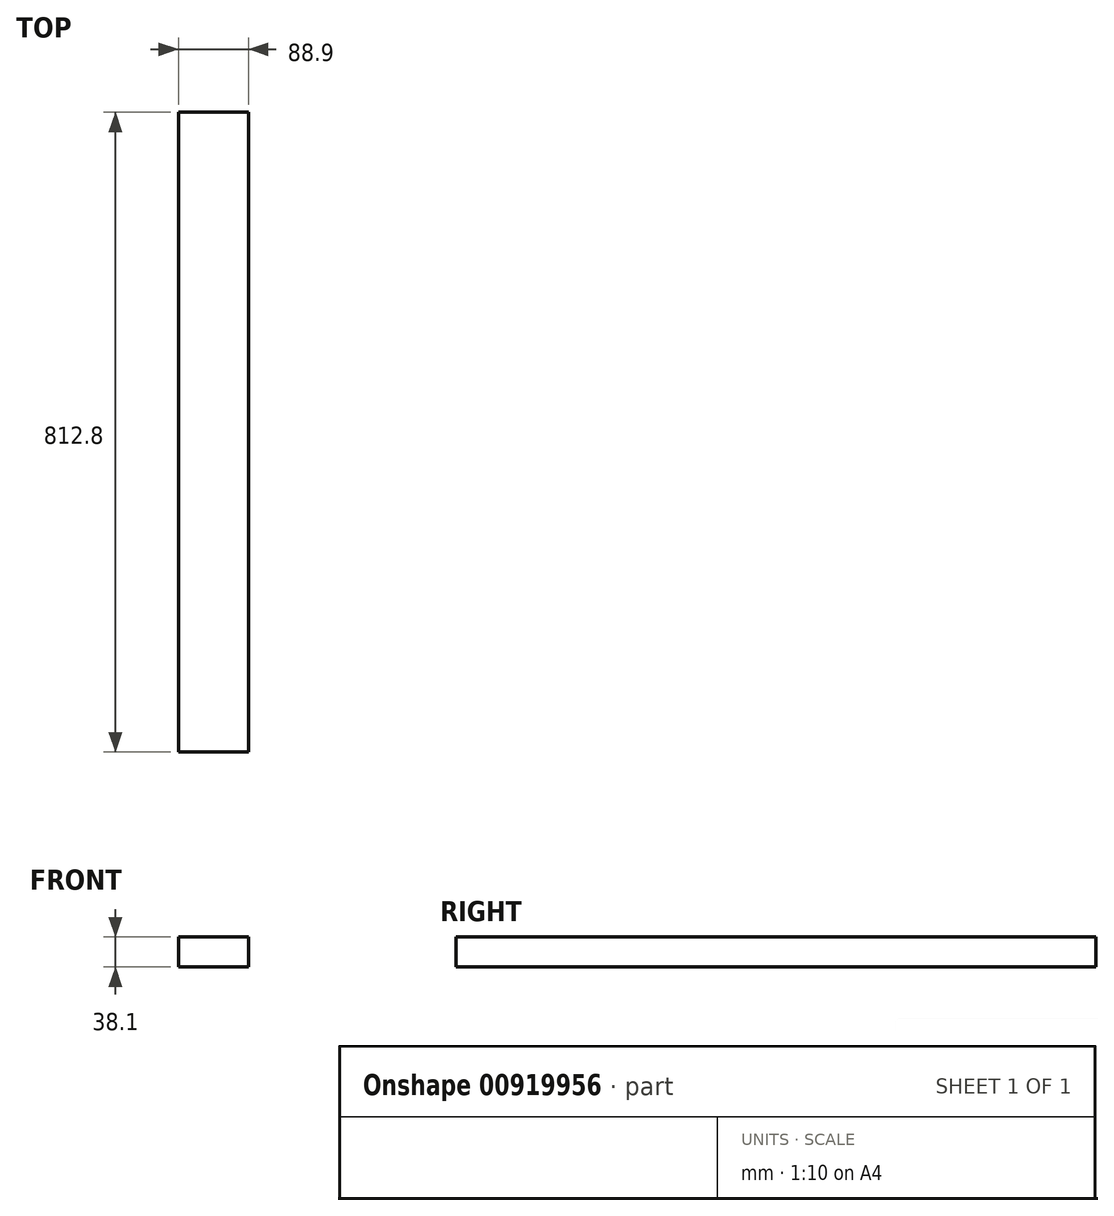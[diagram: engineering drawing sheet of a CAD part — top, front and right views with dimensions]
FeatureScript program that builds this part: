
annotation { "Feature Type Name" : "Feature", "Feature Type Description" : "" }
export const myFeature = defineFeature(function(context is Context, id is Id, definition is map)
    precondition{}
    {
        {
            var Q0;
            Q0=qCreatedBy(makeId("Front.planeOp"),FACE);
            var sketch = newSketch(context, id + "F0", { "sketchPlane" : qUnion([Q0])});
            skLineSegment(sketch, "E0.bottom", {"start": v(44.45, -19.05) * mm, "end": v(-44.45, -19.05) * mm});
            skLineSegment(sketch, "E0.top", {"start": v(44.45, 19.05) * mm, "end": v(-44.45, 19.05) * mm});
            skLineSegment(sketch, "E0.left", {"start": v(44.45, -19.05) * mm, "end": v(44.45, 19.05) * mm});
            skLineSegment(sketch, "E0.right", {"start": v(-44.45, -19.05) * mm, "end": v(-44.45, 19.05) * mm});
            skPoint(sketch, "E0.middle", {"position": v(0, 0) * mm});
            skSolve(sketch);
        }
        {
            var Q0;
            Q0=makeQuery(id+"F0.imprint","IMPRINT",FACE,{"disambiguationData":[TD([[makeQuery(id+"F0.imprint","IMPRINT",EDGE,{"derivedFrom":sQuery(id+"F0.wireOp",EDGE,"E0.bottom")}),-1.0]])]});
            extrude(context, id + "F1", {"entities" : qUnion([Q0]), "endBound" : BoundingType.SYMMETRIC, "depth" : 812.8 * mm, "offsetDistance" : 25.4 * mm});
        }
    });
